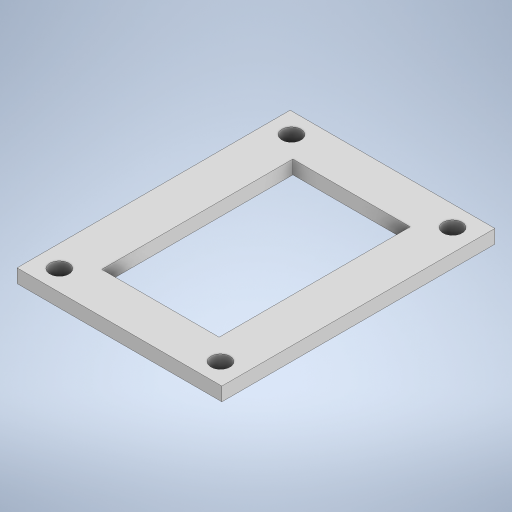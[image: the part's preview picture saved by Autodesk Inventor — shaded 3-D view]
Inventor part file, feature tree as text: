
AUTODESK INVENTOR PART (.ipt)
format: ipt  version: 2023 (Build 270158000, 158)  size: 242,176 bytes
history: native  units: mm
features: other x1, extrude x1, sketch x1
ambient origin geometry x8: Origin, YZ Plane, XZ Plane, XY Plane, X Axis, Y Axis, Z Axis, Center Point
bodies: Body1 (feature_tree)
feature tree (3):
  other  "Sólido1"
  extrude  "Extrusión1"  Depth=5.0mm TaperAngle=0.0deg
  sketch  "Boceto1"  dims[d0=75.0mm d1=15.0mm d2=5.0mm d3=0.0mm]
